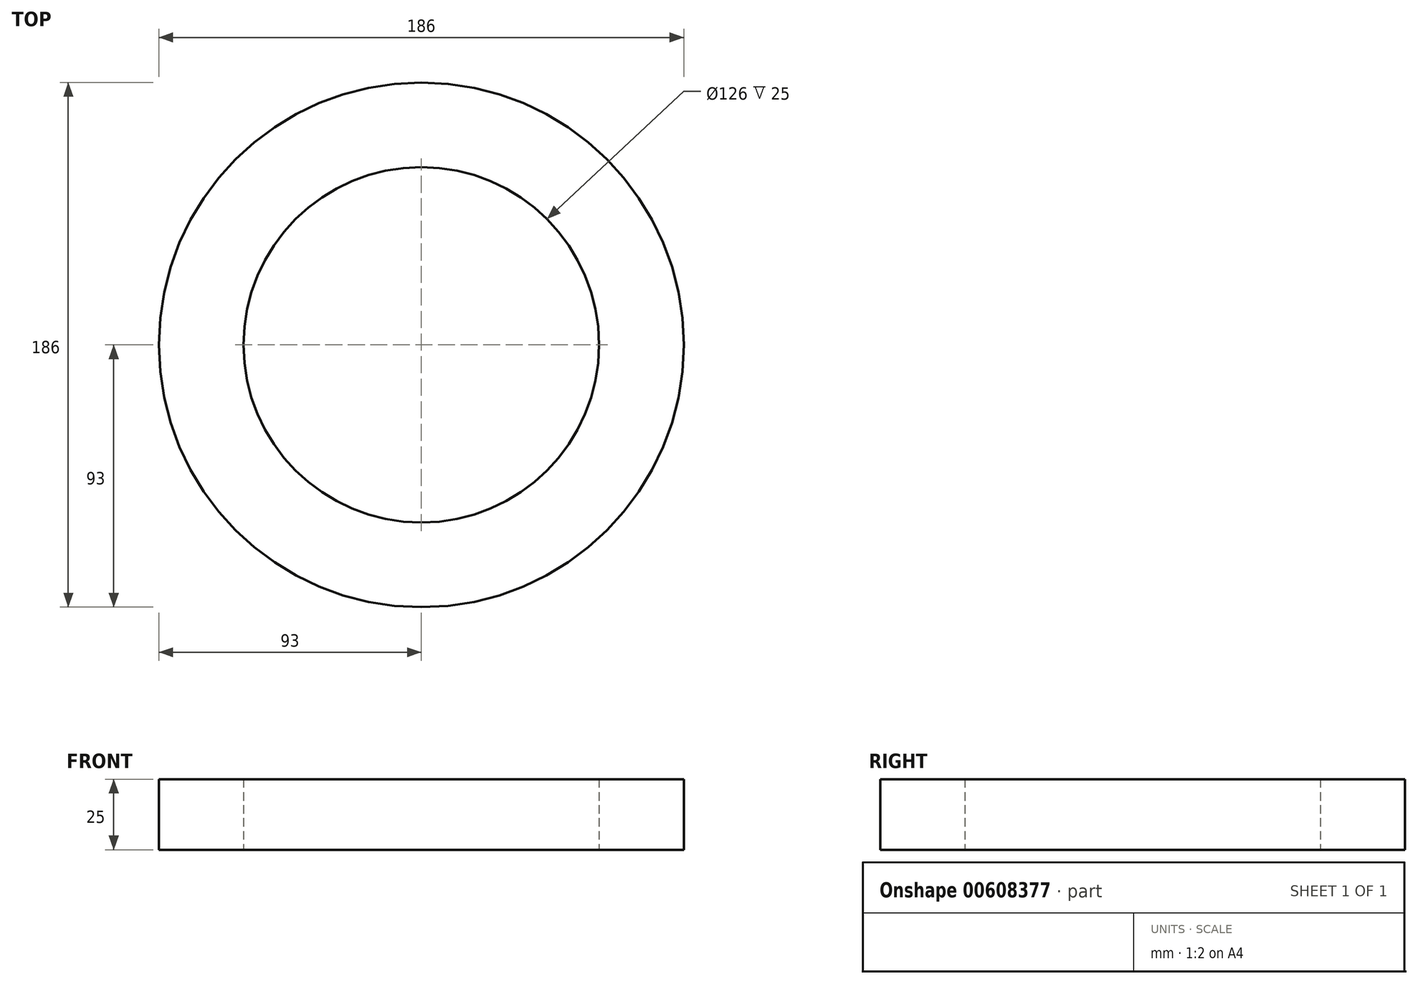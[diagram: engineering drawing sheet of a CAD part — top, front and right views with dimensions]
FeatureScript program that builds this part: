
annotation { "Feature Type Name" : "Feature", "Feature Type Description" : "" }
export const myFeature = defineFeature(function(context is Context, id is Id, definition is map)
    precondition{}
    {
        {
            var Q0;
            Q0=qCreatedBy(makeId("Top.planeOp"), FACE);
            var sketch = newSketch(context, id + "F0", { "sketchPlane" : qUnion([Q0])});
            skCircle(sketch, "E0", {"center": v(0, 0) * mm, "radius": 93 * mm});
            skCircle(sketch, "E1", {"center": v(0, 0) * mm, "radius": 63 * mm});
            skSolve(sketch);
        }
        {
            var Q0;
            Q0 = qSketchRegion(id + "F0", true);
            extrude(context, id + "F1", {"entities" : qUnion([Q0]), "depth" : 25 * mm, "offsetDistance" : 25 * mm});
        }
    });
